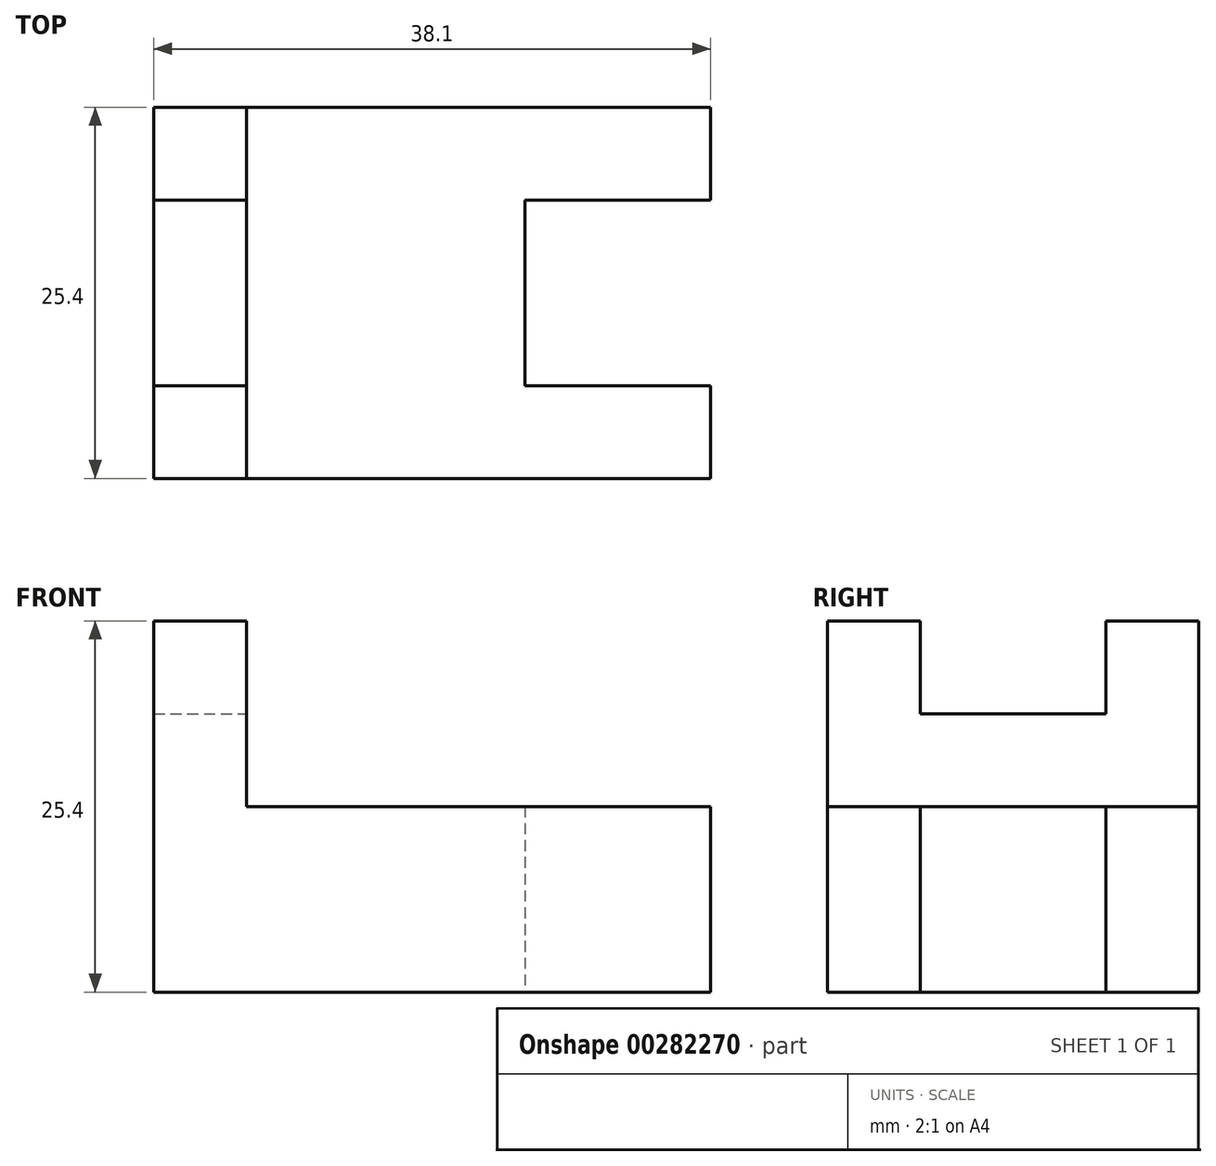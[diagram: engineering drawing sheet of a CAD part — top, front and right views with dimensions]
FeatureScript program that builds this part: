
annotation { "Feature Type Name" : "Feature", "Feature Type Description" : "" }
export const myFeature = defineFeature(function(context is Context, id is Id, definition is map)
    precondition{}
    {
        {
            var Q0;
            Q0=qCreatedBy(makeId("Top.planeOp"),FACE);
            var sketch = newSketch(context, id + "F0", { "sketchPlane" : qUnion([Q0])});
            skLineSegment(sketch, "E0", {"start": v(0, 0) * mm, "end": v(38.1, 0) * mm});
            skLineSegment(sketch, "E1", {"start": v(38.1, 0) * mm, "end": v(38.1, 6.35) * mm});
            skLineSegment(sketch, "E2", {"start": v(38.1, 6.35) * mm, "end": v(25.4, 6.35) * mm});
            skLineSegment(sketch, "E3", {"start": v(25.4, 6.35) * mm, "end": v(25.4, 19.05) * mm});
            skLineSegment(sketch, "E4", {"start": v(25.4, 19.05) * mm, "end": v(38.1, 19.05) * mm});
            skLineSegment(sketch, "E5", {"start": v(38.1, 19.05) * mm, "end": v(38.1, 25.4) * mm});
            skLineSegment(sketch, "E6", {"start": v(38.1, 25.4) * mm, "end": v(0, 25.4) * mm});
            skLineSegment(sketch, "E7", {"start": v(0, 25.4) * mm, "end": v(0, 0) * mm});
            skSolve(sketch);
        }
        {
            var Q0;
            Q0 = qSketchRegion(id + "F0", true);
            extrude(context, id + "F1", {"entities" : qUnion([Q0]), "depth" : 12.7 * mm});
        }
        {
            var Q0;
            Q0=makeQuery(id+"F1.opExtrude","CAP_FACE",FACE,{"disambiguationData":[OSD([sQuery(id+"F0.wireOp",EDGE,"E0"),sQuery(id+"F0.wireOp",EDGE,"E1"),sQuery(id+"F0.wireOp",EDGE,"E2"),sQuery(id+"F0.wireOp",EDGE,"E3"),sQuery(id+"F0.wireOp",EDGE,"E4"),sQuery(id+"F0.wireOp",EDGE,"E5"),sQuery(id+"F0.wireOp",EDGE,"E6"),sQuery(id+"F0.wireOp",EDGE,"E7")])],"isStart":false});
            var sketch = newSketch(context, id + "F2", { "sketchPlane" : qUnion([Q0])});
            skLineSegment(sketch, "E8.bottom", {"start": v(0, 0) * mm, "end": v(6.35, 0) * mm});
            skLineSegment(sketch, "E8.top", {"start": v(0, 25.4) * mm, "end": v(6.35, 25.4) * mm});
            skLineSegment(sketch, "E8.left", {"start": v(0, 0) * mm, "end": v(0, 25.4) * mm});
            skLineSegment(sketch, "E8.right", {"start": v(6.35, 0) * mm, "end": v(6.35, 25.4) * mm});
            skSolve(sketch);
        }
        {
            var Q0;
            Q0 = qSketchRegion(id + "F2", true);
            extrude(context, id + "F3", {"entities" : qUnion([Q0]), "operationType" : NewBodyOperationType.ADD, "depth" : 6.35 * mm});
        }
        {
            var Q0;
            Q0=makeQuery(id+"F3.opExtrude","CAP_FACE",FACE,{"disambiguationData":[OSD([sQuery(id+"F2.wireOp",EDGE,"E8.bottom"),sQuery(id+"F2.wireOp",EDGE,"E8.top"),sQuery(id+"F2.wireOp",EDGE,"E8.left"),sQuery(id+"F2.wireOp",EDGE,"E8.right")])],"isStart":false});
            var sketch = newSketch(context, id + "F4", { "sketchPlane" : qUnion([Q0])});
            skLineSegment(sketch, "E9.bottom", {"start": v(0, 0) * mm, "end": v(6.35, 0) * mm});
            skLineSegment(sketch, "E9.top", {"start": v(0, 6.35) * mm, "end": v(6.35, 6.35) * mm});
            skLineSegment(sketch, "E9.left", {"start": v(0, 0) * mm, "end": v(0, 6.35) * mm});
            skLineSegment(sketch, "E9.right", {"start": v(6.35, 0) * mm, "end": v(6.35, 6.35) * mm});
            skSolve(sketch);
        }
        {
            var Q0;
            Q0 = qSketchRegion(id + "F4", true);
            extrude(context, id + "F5", {"entities" : qUnion([Q0]), "operationType" : NewBodyOperationType.ADD, "depth" : 6.35 * mm});
        }
        {
            var Q0;
            Q0=makeQuery(id+"F3.opExtrude","CAP_FACE",FACE,{"disambiguationData":[OSD([sQuery(id+"F2.wireOp",EDGE,"E8.bottom"),sQuery(id+"F2.wireOp",EDGE,"E8.top"),sQuery(id+"F2.wireOp",EDGE,"E8.left"),sQuery(id+"F2.wireOp",EDGE,"E8.right")])],"isStart":false});
            var sketch = newSketch(context, id + "F6", { "sketchPlane" : qUnion([Q0])});
            skLineSegment(sketch, "E10.bottom", {"start": v(0, 25.4) * mm, "end": v(6.35, 25.4) * mm});
            skLineSegment(sketch, "E10.top", {"start": v(0, 19.05) * mm, "end": v(6.35, 19.05) * mm});
            skLineSegment(sketch, "E10.left", {"start": v(0, 25.4) * mm, "end": v(0, 19.05) * mm});
            skLineSegment(sketch, "E10.right", {"start": v(6.35, 25.4) * mm, "end": v(6.35, 19.05) * mm});
            skSolve(sketch);
        }
        {
            var Q0;
            Q0 = qSketchRegion(id + "F6", true);
            extrude(context, id + "F7", {"entities" : qUnion([Q0]), "operationType" : NewBodyOperationType.ADD, "depth" : 6.35 * mm});
        }
    });
